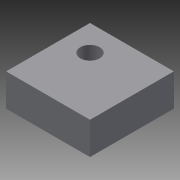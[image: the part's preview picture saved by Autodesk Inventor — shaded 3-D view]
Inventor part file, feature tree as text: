
AUTODESK INVENTOR PART (.ipt)
format: ipt  version: 2015 SP2 (Build 190223200, 223)  size: 78,848 bytes
history: native  units: mm
features: sketch x2, extrude x1, hole x1
ambient origin geometry x8: Origin, YZ Plane, XZ Plane, XY Plane, X Axis, Y Axis, Z Axis, Center Point
bodies: Solid1 (feature_tree)
feature tree (4):
  extrude  "Extrusion1"  Depth=13.0mm
  hole  "Hole1"  [1 undecoded]
  sketch  "Sketch1"  dims[d0=13.0mm d1=13.0mm]
  sketch  "Sketch2"  dims[d2=5.0mm d3=0.0mm d4=4.0mm d5=4.0mm d6=3.0mm d7=6.0mm d8=4.0mm d9=2.0mm d10=90.0deg d11=8.0mm d12=20.594885mm]
note: 1 required parameter value undecoded (feature->parameter linkage not recoverable at this tier; creation-order binding heuristic only, values carry confidence <= 0.55)
